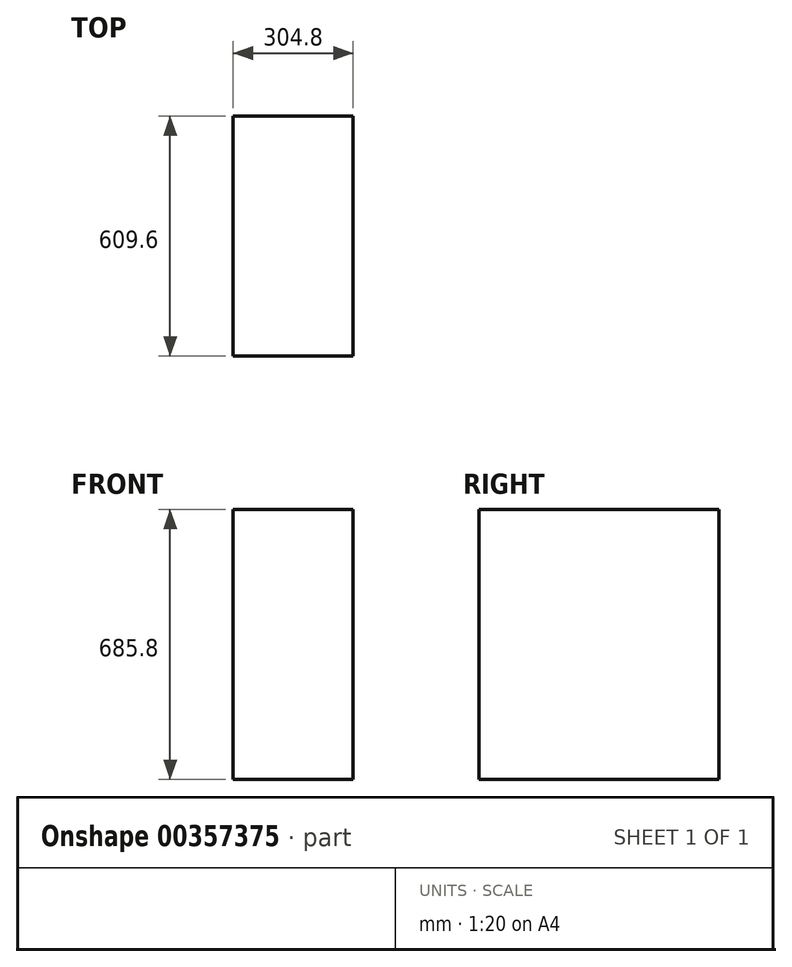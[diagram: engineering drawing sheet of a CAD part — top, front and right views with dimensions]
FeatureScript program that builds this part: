
annotation { "Feature Type Name" : "Feature", "Feature Type Description" : "" }
export const myFeature = defineFeature(function(context is Context, id is Id, definition is map)
    precondition{}
    {
        {
            var Q0;
            Q0=qCreatedBy(makeId("Top.planeOp"),FACE);
            var sketch = newSketch(context, id + "F0", { "sketchPlane" : qUnion([Q0])});
            skLineSegment(sketch, "E0.bottom", {"start": v(-152.4, -304.8) * mm, "end": v(152.4, -304.8) * mm});
            skLineSegment(sketch, "E0.top", {"start": v(-152.4, 304.8) * mm, "end": v(152.4, 304.8) * mm});
            skLineSegment(sketch, "E0.left", {"start": v(-152.4, -304.8) * mm, "end": v(-152.4, 304.8) * mm});
            skLineSegment(sketch, "E0.right", {"start": v(152.4, -304.8) * mm, "end": v(152.4, 304.8) * mm});
            skPoint(sketch, "E0.middle", {"position": v(0, 0) * mm});
            skSolve(sketch);
        }
        {
            var Q0;
            Q0 = qSketchRegion(id + "F0", true);
            extrude(context, id + "F1", {"entities" : qUnion([Q0]), "depth" : 685.8 * mm});
        }
    });
